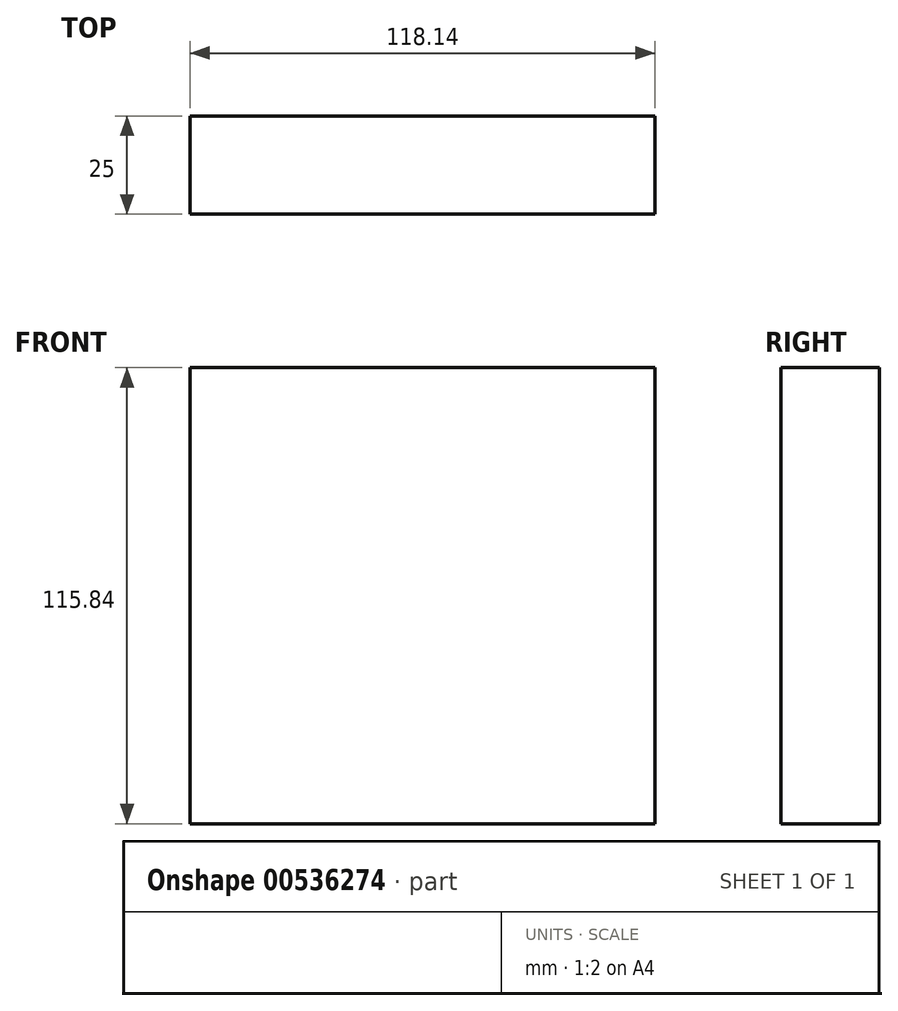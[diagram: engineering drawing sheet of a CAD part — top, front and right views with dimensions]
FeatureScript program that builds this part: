
annotation { "Feature Type Name" : "Feature", "Feature Type Description" : "" }
export const myFeature = defineFeature(function(context is Context, id is Id, definition is map)
    precondition{}
    {
        {
            var Q0;
            Q0=qCreatedBy(makeId("Front.planeOp"),FACE);
            var sketch = newSketch(context, id + "F0", { "sketchPlane" : qUnion([Q0])});
            skLineSegment(sketch, "E0.bottom", {"start": v(-58.42, -15.9) * mm, "end": v(-176.56, -15.9) * mm});
            skLineSegment(sketch, "E0.top", {"start": v(-58.42, 99.95) * mm, "end": v(-176.56, 99.95) * mm});
            skLineSegment(sketch, "E0.left", {"start": v(-58.42, -15.9) * mm, "end": v(-58.42, 99.95) * mm});
            skLineSegment(sketch, "E0.right", {"start": v(-176.56, -15.9) * mm, "end": v(-176.56, 99.95) * mm});
            skPoint(sketch, "E0.middle", {"position": v(-117.49, 42.03) * mm});
            skSolve(sketch);
        }
        {
            var Q0;
            Q0 = qSketchRegion(id + "F0", true);
            extrude(context, id + "F1", {"entities" : qUnion([Q0]), "depth" : 25 * mm, "offsetDistance" : 25 * mm});
        }
    });
